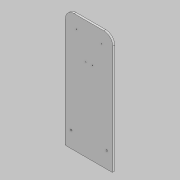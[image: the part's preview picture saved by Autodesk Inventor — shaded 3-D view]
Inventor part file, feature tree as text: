
AUTODESK INVENTOR PART (.ipt)
format: ipt  version: 2020 (Build 240168000, 168)  size: 136,704 bytes
history: native  units: in
note: dims shown in document units (in); Inventor stores cm internally (conversion verified against a paired STEP export)
features: sketch x3, fillet x2, hole x2, extrude x1
ambient origin geometry x8: Origin, YZ Plane, XZ Plane, XY Plane, X Axis, Y Axis, Z Axis, Center Point
bodies: Solid1 (feature_tree)
feature tree (8):
  extrude  "Extrusion1"  Depth=9.4488in
  fillet  "Fillet1"  Radius=4.7244in
  hole  "Hole1"  [1 undecoded]
  hole  "Hole2"  [1 undecoded]
  fillet  "Fillet2"  Radius=3.5433in
  sketch  "Sketch1"  dims[d0=23.622in d1=9.4488in d2=4.7244in]
  sketch  "Sketch2"  dims[d3=0.3937in d4=0.0in d5=1.7717in]
  sketch  "Sketch3"  dims[d8=3.2283in d9=3.2283in d10=0.315in d11=0.2362in d12=0.5512in d13=0.2756in d14=90.0deg d15=2.3622in d16=0.0in d17=3.5433in d18=3.5433in d19=0.6693in d20=0.6693in d21=2.5in d22=2.5in d23=2.4789in d24=2.4789in d25=4.731in d26=4.6641in d27=0.1575in d28=0.2362in d29=0.1575in d30=0.0787in d31=90.0deg d32=0.315in d33=0.8108in d34=0.0787in]
note: 2 required parameter values undecoded (feature->parameter linkage not recoverable at this tier; creation-order binding heuristic only, values carry confidence <= 0.55)
